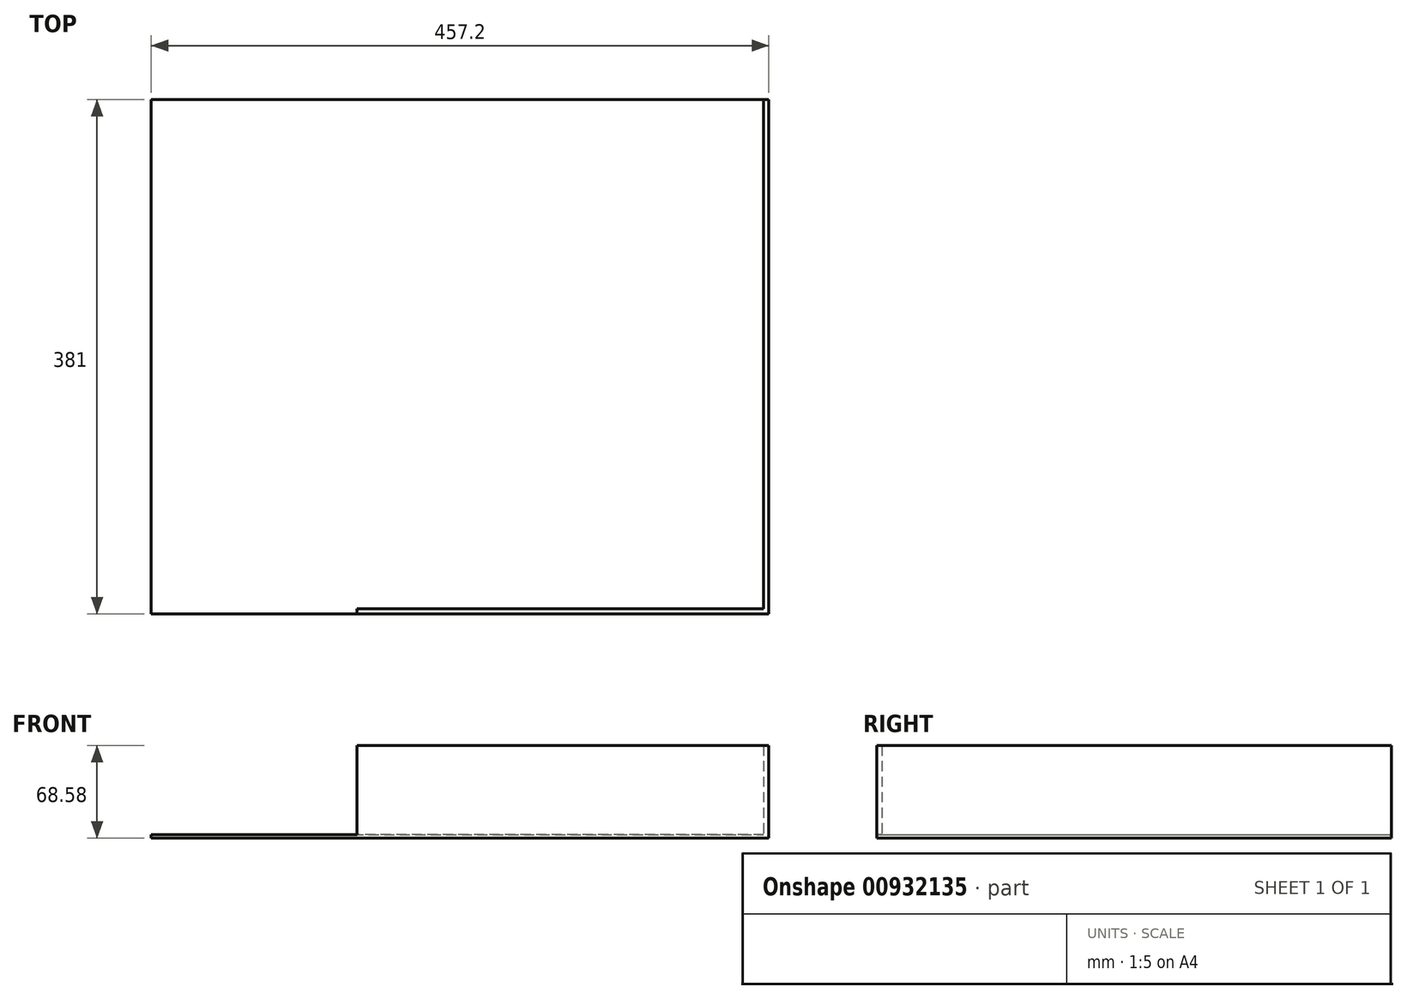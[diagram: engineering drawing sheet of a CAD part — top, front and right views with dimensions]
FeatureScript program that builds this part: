
annotation { "Feature Type Name" : "Feature", "Feature Type Description" : "" }
export const myFeature = defineFeature(function(context is Context, id is Id, definition is map)
    precondition{}
    {
        {
            var Q0;
            Q0=qCreatedBy(makeId("Top.planeOp"),FACE);
            var sketch = newSketch(context, id + "F0", { "sketchPlane" : qUnion([Q0])});
            skLineSegment(sketch, "E0.bottom", {"start": v(0, 0) * mm, "end": v(457.2, 0) * mm});
            skLineSegment(sketch, "E0.top", {"start": v(0, 381) * mm, "end": v(457.2, 381) * mm});
            skLineSegment(sketch, "E0.left", {"start": v(0, 0) * mm, "end": v(0, 381) * mm});
            skLineSegment(sketch, "E0.right", {"start": v(457.2, 0) * mm, "end": v(457.2, 381) * mm});
            skSolve(sketch);
        }
        {
            var Q0;
            Q0=makeQuery(id+"F0.imprint","IMPRINT",FACE,{"disambiguationData":[TD([[makeQuery(id+"F0.imprint","IMPRINT",EDGE,{"derivedFrom":sQuery(id+"F0.wireOp",EDGE,"E0.bottom")}),1.0]])]});
            extrude(context, id + "F1", {"entities" : qUnion([Q0]), "depth" : 2.54 * mm, "offsetDistance" : 25.4 * mm});
        }
        {
            var Q0;
            Q0=qCreatedBy(makeId("Top.planeOp"),FACE);
            var sketch = newSketch(context, id + "F2", { "sketchPlane" : qUnion([Q0])});
            skLineSegment(sketch, "E1", {"start": v(457.2, 0) * mm, "end": v(152.4, 0) * mm});
            skLineSegment(sketch, "E2", {"start": v(152.4, 0) * mm, "end": v(152.4, 3.8) * mm});
            skLineSegment(sketch, "E3", {"start": v(152.4, 3.8) * mm, "end": v(457.2, 3.8) * mm});
            skLineSegment(sketch, "E4", {"start": v(457.2, 3.8) * mm, "end": v(457.2, 0) * mm});
            skSolve(sketch);
        }
        {
            var Q0;
            Q0 = qSketchRegion(id + "F2", true);
            extrude(context, id + "F3", {"entities" : qUnion([Q0]), "operationType" : NewBodyOperationType.ADD, "depth" : 68.58 * mm, "offsetDistance" : 25.4 * mm});
        }
        {
            var Q0;
            Q0=makeQuery(id+"F1.opExtrude","CAP_FACE",FACE,{"disambiguationData":[OSD([sQuery(id+"F0.wireOp",EDGE,"E0.bottom"),sQuery(id+"F0.wireOp",EDGE,"E0.top"),sQuery(id+"F0.wireOp",EDGE,"E0.left"),sQuery(id+"F0.wireOp",EDGE,"E0.right")])],"isStart":false});
            var sketch = newSketch(context, id + "F4", { "sketchPlane" : qUnion([Q0])});
            skLineSegment(sketch, "E5.bottom", {"start": v(457.2, 3.8) * mm, "end": v(453.4, 3.8) * mm});
            skLineSegment(sketch, "E5.top", {"start": v(457.2, 384.8) * mm, "end": v(453.4, 384.8) * mm});
            skLineSegment(sketch, "E5.left", {"start": v(457.2, 3.8) * mm, "end": v(457.2, 384.8) * mm});
            skLineSegment(sketch, "E5.right", {"start": v(453.4, 3.8) * mm, "end": v(453.4, 384.8) * mm});
            skSolve(sketch);
        }
        {
            var Q0;
            {var subQ0=sQuery(id+"F4.wireOp",EDGE,"E5.bottom");Q0=makeQuery(id+"F4.imprint","IMPRINT",FACE,{"disambiguationData":[TD([[makeQuery(id+"F4.imprint","IMPRINT",EDGE,{"derivedFrom":subQ0}),-1.0]])]});}
            extrude(context, id + "F5", {"entities" : qUnion([Q0]), "operationType" : NewBodyOperationType.ADD, "depth" : 66.04 * mm, "offsetDistance" : 25.4 * mm});
        }
    });
